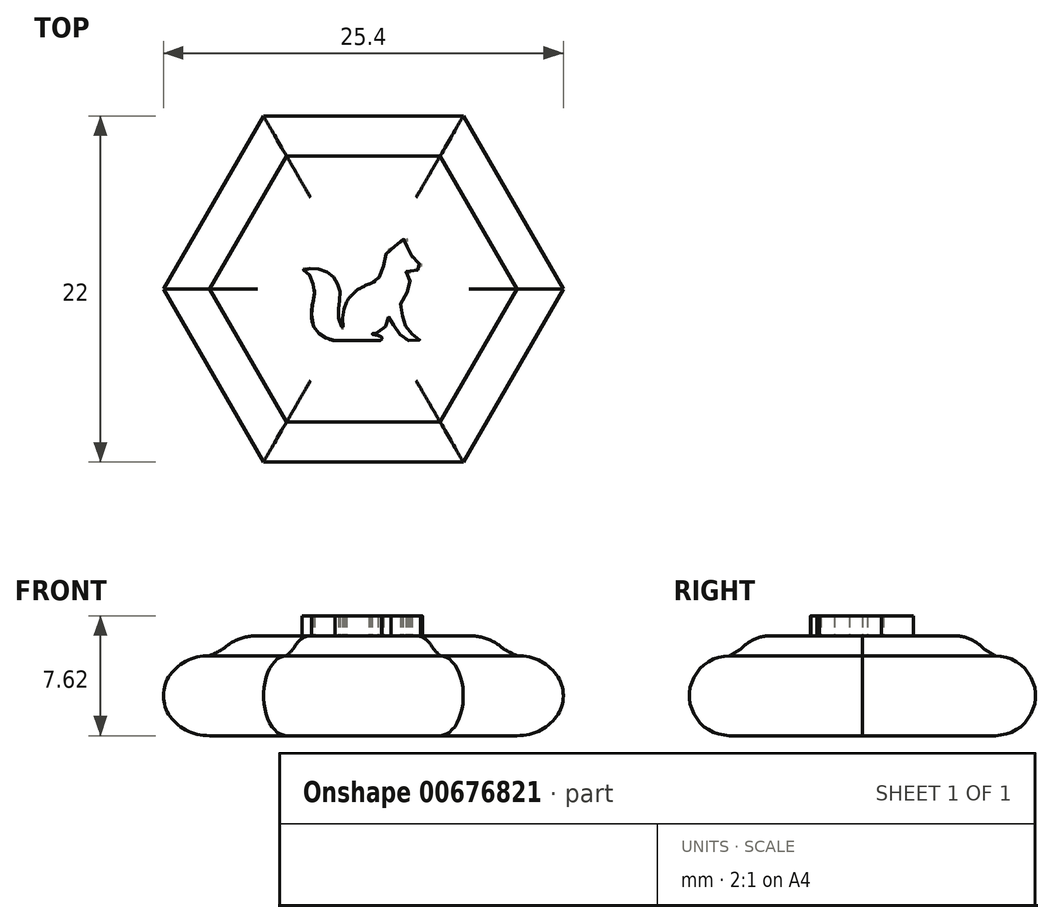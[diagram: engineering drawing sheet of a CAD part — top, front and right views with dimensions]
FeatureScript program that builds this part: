
annotation { "Feature Type Name" : "Feature", "Feature Type Description" : "" }
export const myFeature = defineFeature(function(context is Context, id is Id, definition is map)
    precondition{}
    {
        {
            var Q0;
            Q0=qCreatedBy(makeId("Front.planeOp"),FACE);
            var sketch = newSketch(context, id + "F0", { "sketchPlane" : qUnion([Q0])});
            skLineSegment(sketch, "E0", {"start": v(0, 0) * mm, "end": v(-10.16, 0) * mm});
            skLineSegment(sketch, "E1", {"start": v(-10.16, 0) * mm, "end": v(-10.16, 5.08) * mm, "construction": true});
            skLineSegment(sketch, "E2", {"start": v(10.16, 5.08) * mm, "end": v(10.16, 0) * mm, "construction": true});
            skLineSegment(sketch, "E3", {"start": v(10.16, 0) * mm, "end": v(0, 0) * mm});
            skLineSegment(sketch, "E4", {"start": v(-10.16, 5.08) * mm, "end": v(-9.2, 5.08) * mm, "construction": true});
            skLineSegment(sketch, "E5", {"start": v(-9.2, 5.08) * mm, "end": v(-8.9, 5.08) * mm, "construction": true});
            skLineSegment(sketch, "E6", {"start": v(-9.2, 5.08) * mm, "end": v(-9.2, 5.71) * mm, "construction": true});
            skLineSegment(sketch, "E7", {"start": v(-8.9, 5.08) * mm, "end": v(-8.9, 6.35) * mm, "construction": true});
            skLineSegment(sketch, "E8", {"start": v(10.16, 5.08) * mm, "end": v(9.2, 5.08) * mm, "construction": true});
            skLineSegment(sketch, "E9", {"start": v(9.2, 5.08) * mm, "end": v(8.89, 5.08) * mm, "construction": true});
            skLineSegment(sketch, "E10", {"start": v(8.89, 5.08) * mm, "end": v(8.89, 6.35) * mm, "construction": true});
            skLineSegment(sketch, "E11", {"start": v(9.2, 5.08) * mm, "end": v(9.2, 5.72) * mm, "construction": true});
            skFitSpline(sketch, "E12", {"points": [v(-10.16, 5.08) * mm, v(-9.2, 5.71) * mm, v(-8.9, 6.35) * mm], "startDerivative": vector(7.31, 1.8) * mm, "endDerivative": vector(2.53, 3.38) * mm});
            skFitSpline(sketch, "E13", {"points": [v(8.89, 6.35) * mm, v(9.2, 5.72) * mm, v(10.16, 5.08) * mm], "startDerivative": vector(2.53, -3.38) * mm, "endDerivative": vector(7.31, -1.8) * mm});
            skLineSegment(sketch, "E14", {"start": v(-7.22, 6.35) * mm, "end": v(7.22, 6.35) * mm});
            skArc(sketch, "E15.filletArc", {"start": v(9.14, 5.47) * mm, "mid": v(8.27, 6.12) * mm, "end": v(7.22, 6.35) * mm});
            skArc(sketch, "E16.filletArc", {"start": v(-7.22, 6.35) * mm, "mid": v(-8.27, 6.12) * mm, "end": v(-9.14, 5.47) * mm});
            skArc(sketch, "E17", {"start": v(10.16, 0) * mm, "mid": v(12.7, 2.54) * mm, "end": v(10.16, 5.08) * mm});
            skArc(sketch, "E18", {"start": v(-10.16, 5.08) * mm, "mid": v(-12.7, 2.54) * mm, "end": v(-10.16, 0) * mm});
            skLineSegment(sketch, "E19", {"start": v(0, 0) * mm, "end": v(0, 6.35) * mm, "construction": true});
            skLineSegment(sketch, "E20", {"start": v(10.16, 2.54) * mm, "end": v(12.7, 2.54) * mm, "construction": true});
            skSolve(sketch);
        }
        {
            var Q0;
            Q0=qSketchRegion(id+"F0",true);
            extrude(context, id + "F1", {"entities" : qUnion([Q0]), "endBound" : BoundingType.SYMMETRIC, "depth" : 25.4 * mm, "offsetDistance" : 25.4 * mm});
        }
        {
            var Q0;
            Q0=qCreatedBy(makeId("Right.planeOp"),FACE);
            var sketch = newSketch(context, id + "F2", { "sketchPlane" : qUnion([Q0])});
            skLineSegment(sketch, "E21", {"start": v(0, 0) * mm, "end": v(-8.46, 0) * mm, "construction": true});
            skLineSegment(sketch, "E22", {"start": v(0, 0) * mm, "end": v(8.46, 0) * mm, "construction": true});
            skLineSegment(sketch, "E23", {"start": v(-8.46, 0) * mm, "end": v(-8.46, 5.08) * mm, "construction": true});
            skLineSegment(sketch, "E24", {"start": v(8.46, 0) * mm, "end": v(8.46, 5.08) * mm, "construction": true});
            skLineSegment(sketch, "E25", {"start": v(-8.46, 5.08) * mm, "end": v(-7.5, 5.08) * mm, "construction": true});
            skLineSegment(sketch, "E26", {"start": v(-7.5, 5.08) * mm, "end": v(-7.19, 5.08) * mm, "construction": true});
            skLineSegment(sketch, "E27", {"start": v(-7.5, 5.08) * mm, "end": v(-7.5, 5.72) * mm, "construction": true});
            skLineSegment(sketch, "E28", {"start": v(8.46, 5.08) * mm, "end": v(7.5, 5.08) * mm, "construction": true});
            skLineSegment(sketch, "E29", {"start": v(7.5, 5.08) * mm, "end": v(7.19, 5.08) * mm, "construction": true});
            skLineSegment(sketch, "E30", {"start": v(7.5, 5.08) * mm, "end": v(7.5, 5.72) * mm, "construction": true});
            skArc(sketch, "E31", {"start": v(8.46, 0) * mm, "mid": v(11, 2.54) * mm, "end": v(8.46, 5.08) * mm});
            skArc(sketch, "E32", {"start": v(-8.46, 5.08) * mm, "mid": v(-11, 2.54) * mm, "end": v(-8.46, 0) * mm});
            skPoint(sketch, "E33.visualSharp", {"position": v(-7.19, 6.35) * mm});
            skLineSegment(sketch, "E34", {"start": v(-7.19, 5.08) * mm, "end": v(-7.19, 6.35) * mm, "construction": true});
            skPoint(sketch, "E35.visualSharp", {"position": v(7.19, 6.35) * mm});
            skLineSegment(sketch, "E36", {"start": v(7.19, 5.08) * mm, "end": v(7.19, 6.35) * mm, "construction": true});
            skLineSegment(sketch, "E37", {"start": v(0, 0) * mm, "end": v(0, 6.35) * mm, "construction": true});
            skLineSegment(sketch, "E38", {"start": v(18.44, 6.35) * mm, "end": v(18.44, 0) * mm});
            skLineSegment(sketch, "E39", {"start": v(-18.44, 6.35) * mm, "end": v(-18.44, 0) * mm});
            skLineSegment(sketch, "E40", {"start": v(-8.46, 0) * mm, "end": v(-18.44, 0) * mm});
            skLineSegment(sketch, "E41", {"start": v(-8.46, 2.54) * mm, "end": v(-11, 2.54) * mm, "construction": true});
            skLineSegment(sketch, "E42", {"start": v(18.44, 0) * mm, "end": v(8.46, 0) * mm});
            skLineSegment(sketch, "E43", {"start": v(0, 0) * mm, "end": v(0, 0) * mm});
            skLineSegment(sketch, "E44", {"start": v(-5.82, 6.35) * mm, "end": v(5.82, 6.35) * mm});
            skFitSpline(sketch, "E45", {"points": [v(-8.46, 5.08) * mm, v(-7.5, 5.71) * mm, v(-7.19, 6.35) * mm], "startDerivative": vector(1.98, 1.05) * mm, "endDerivative": vector(0.5, 1.5) * mm});
            skFitSpline(sketch, "E46", {"points": [v(7.19, 6.35) * mm, v(7.5, 5.71) * mm, v(8.46, 5.08) * mm], "startDerivative": vector(0.5, -1.5) * mm, "endDerivative": vector(1.98, -1.05) * mm});
            skArc(sketch, "E47.filletArc", {"start": v(-5.82, 6.35) * mm, "mid": v(-6.76, 6.17) * mm, "end": v(-7.58, 5.64) * mm});
            skArc(sketch, "E48.filletArc", {"start": v(7.58, 5.64) * mm, "mid": v(6.76, 6.17) * mm, "end": v(5.82, 6.35) * mm});
            skLineSegment(sketch, "E49", {"start": v(-18.44, 6.35) * mm, "end": v(-5.82, 6.35) * mm});
            skLineSegment(sketch, "E50", {"start": v(5.82, 6.35) * mm, "end": v(18.44, 6.35) * mm});
            skSolve(sketch);
        }
        {
            var Q0;
            Q0=qSketchRegion(id+"F2",true);
            extrude(context, id + "F3", {"entities" : qUnion([Q0]), "operationType" : NewBodyOperationType.REMOVE, "endBound" : BoundingType.SYMMETRIC, "depth" : 25.4 * mm, "offsetDistance" : 25.4 * mm});
        }
        {
            var Q0;
            Q0=sQuery(id+"F0.wireOp",EDGE,"E19");
            cPlane(context, id + "F4", {"entities" : qUnion([Q0]), "cplaneType" : CPlaneType.LINE_ANGLE, "offset" : 25.4 * mm, "angle" : 120 * degree, "width" : 152.4 * mm, "height" : 152.4 * mm});
        }
        {
            var Q0;
            Q0=qCreatedBy(id+"F4.planeOp",FACE);
            var sketch = newSketch(context, id + "F5", { "sketchPlane" : qUnion([Q0])});
            skLineSegment(sketch, "E51", {"start": v(0, 0) * mm, "end": v(-8.46, 0) * mm, "construction": true});
            skLineSegment(sketch, "E52", {"start": v(0, 0) * mm, "end": v(8.46, 0) * mm, "construction": true});
            skLineSegment(sketch, "E53", {"start": v(-8.46, 0) * mm, "end": v(-8.46, 5.08) * mm, "construction": true});
            skLineSegment(sketch, "E54", {"start": v(8.46, 0) * mm, "end": v(8.46, 5.08) * mm, "construction": true});
            skLineSegment(sketch, "E55", {"start": v(-8.46, 5.08) * mm, "end": v(-7.5, 5.08) * mm, "construction": true});
            skLineSegment(sketch, "E56", {"start": v(-7.5, 5.08) * mm, "end": v(-7.19, 5.08) * mm, "construction": true});
            skLineSegment(sketch, "E57", {"start": v(-7.5, 5.08) * mm, "end": v(-7.5, 5.72) * mm, "construction": true});
            skLineSegment(sketch, "E58", {"start": v(8.46, 5.08) * mm, "end": v(7.5, 5.08) * mm, "construction": true});
            skLineSegment(sketch, "E59", {"start": v(7.5, 5.08) * mm, "end": v(7.19, 5.08) * mm, "construction": true});
            skLineSegment(sketch, "E60", {"start": v(7.5, 5.08) * mm, "end": v(7.5, 5.72) * mm, "construction": true});
            skArc(sketch, "E61", {"start": v(8.46, 0) * mm, "mid": v(11, 2.54) * mm, "end": v(8.46, 5.08) * mm});
            skArc(sketch, "E62", {"start": v(-8.46, 5.08) * mm, "mid": v(-11, 2.54) * mm, "end": v(-8.46, 0) * mm});
            skPoint(sketch, "E63.visualSharp", {"position": v(-7.19, 6.35) * mm});
            skLineSegment(sketch, "E64", {"start": v(-7.19, 5.08) * mm, "end": v(-7.19, 6.35) * mm, "construction": true});
            skPoint(sketch, "E65.visualSharp", {"position": v(7.19, 6.35) * mm});
            skLineSegment(sketch, "E66", {"start": v(7.19, 5.08) * mm, "end": v(7.19, 6.35) * mm, "construction": true});
            skLineSegment(sketch, "E67", {"start": v(0, 0) * mm, "end": v(0, 6.35) * mm, "construction": true});
            skLineSegment(sketch, "E68", {"start": v(18.44, 6.35) * mm, "end": v(18.44, 0) * mm});
            skLineSegment(sketch, "E69", {"start": v(-18.44, 6.35) * mm, "end": v(-18.44, 0) * mm});
            skLineSegment(sketch, "E70", {"start": v(-8.46, 0) * mm, "end": v(-18.44, 0) * mm});
            skLineSegment(sketch, "E71", {"start": v(-8.46, 2.54) * mm, "end": v(-11, 2.54) * mm, "construction": true});
            skLineSegment(sketch, "E72", {"start": v(18.44, 0) * mm, "end": v(8.46, 0) * mm});
            skLineSegment(sketch, "E73", {"start": v(0, 0) * mm, "end": v(0, 0) * mm});
            skLineSegment(sketch, "E74", {"start": v(-5.82, 6.35) * mm, "end": v(5.82, 6.35) * mm});
            skFitSpline(sketch, "E75", {"points": [v(-8.46, 5.08) * mm, v(-7.5, 5.71) * mm, v(-7.19, 6.35) * mm], "startDerivative": vector(1.98, 1.05) * mm, "endDerivative": vector(0.5, 1.5) * mm});
            skFitSpline(sketch, "E76", {"points": [v(7.19, 6.35) * mm, v(7.5, 5.71) * mm, v(8.46, 5.08) * mm], "startDerivative": vector(0.5, -1.5) * mm, "endDerivative": vector(1.98, -1.05) * mm});
            skArc(sketch, "E77.filletArc", {"start": v(-5.82, 6.35) * mm, "mid": v(-6.76, 6.17) * mm, "end": v(-7.58, 5.64) * mm});
            skArc(sketch, "E78.filletArc", {"start": v(7.58, 5.64) * mm, "mid": v(6.76, 6.17) * mm, "end": v(5.82, 6.35) * mm});
            skLineSegment(sketch, "E79", {"start": v(-18.44, 6.35) * mm, "end": v(-5.82, 6.35) * mm});
            skLineSegment(sketch, "E80", {"start": v(5.82, 6.35) * mm, "end": v(18.44, 6.35) * mm});
            skSolve(sketch);
        }
        {
            var Q0;
            Q0=qSketchRegion(id+"F5",true);
            var Q1;
            Q1=sQuery(id+"FHUch5MhYWofbFd_1.wireOp",EDGE,"UJUXWhbe-ns99-R938-MBjs-qnEI7qI75ZtX");
            var Q2;
            Q2=sQuery(id+"FHUch5MhYWofbFd_1.wireOp",EDGE,"TGRI2bbO-5mKc-ZYGL-RI2u-ax8UZepCr2S6");
            var Q3;
            Q3=sQuery(id+"FHUch5MhYWofbFd_1.wireOp",EDGE,"3EN97P5a-7fpQ-fkxS-kFIG-O94JdEreBvdc");
            var Q4;
            Q4=sQuery(id+"FHUch5MhYWofbFd_1.wireOp",EDGE,"BLXI86f6-p3FV-xg8e-vcjV-MuaEN1ZbEeBN");
            var Q5;
            Q5=sQuery(id+"FHUch5MhYWofbFd_1.wireOp",EDGE,"K6Pg9hkI-HhUm-eWt8-lgsy-rQcUfMNRkeRX");
            var Q6;
            Q6=sQuery(id+"FHUch5MhYWofbFd_1.wireOp",EDGE,"8MWXePed-qfWZ-9kiI-xQLn-RgFZeWpe4DeW");
            var Q7;
            Q7=sQuery(id+"FHUch5MhYWofbFd_1.wireOp",EDGE,"ujHeR1Bt-oqxH-zWrO-aF7a-1cGxx1oxEC4p");
            var Q8;
            Q8=sQuery(id+"FHUch5MhYWofbFd_1.wireOp",EDGE,"ezDig2bh-fpcZ-qdXg-hfEw-k3bdO8GFTHoY");
            var Q9;
            Q9=sQuery(id+"FHUch5MhYWofbFd_1.wireOp",EDGE,"TL3t9Hpy-tibO-WM6d-k033-ZjCVjvvUcohB");
            var Q10;
            Q10=sQuery(id+"FHUch5MhYWofbFd_1.wireOp",EDGE,"H6XLH3zd-cpDk-JRaX-qujs-Kg6a5HbhHDUq");
            var Q11;
            Q11=sQuery(id+"FHUch5MhYWofbFd_1.wireOp",EDGE,"XlrNxneH-uq2I-L97s-EfPg-StDvBexp0ezL");
            var Q12;
            Q12=sQuery(id+"FHUch5MhYWofbFd_1.wireOp",EDGE,"V9PWrxtB-5fyD-G3Op-kF2t-xwj5HEO20ic1");
            var Q13;
            Q13=sQuery(id+"FHUch5MhYWofbFd_1.wireOp",EDGE,"DBsLzJAx-6rkW-YoXi-OfuC-MLqgEexGkzpa");
            extrude(context, id + "F6", {"entities" : qUnion([Q0]), "operationType" : NewBodyOperationType.REMOVE, "surfaceEntities" : qUnion([Q1, Q2, Q3, Q4, Q5, Q6, Q7, Q8, Q9, Q10, Q11, Q12, Q13]), "endBound" : BoundingType.SYMMETRIC, "oppositeDirection" : true, "depth" : 50.8 * mm, "offsetDistance" : 25.4 * mm});
        }
        {
            var Q0;
            Q0=sQuery(id+"F0.wireOp",EDGE,"E19");
            cPlane(context, id + "F7", {"entities" : qUnion([Q0]), "cplaneType" : CPlaneType.LINE_ANGLE, "offset" : 25.4 * mm, "angle" : 60 * degree, "width" : 152.4 * mm, "height" : 152.4 * mm});
        }
        {
            var Q0;
            Q0=qCreatedBy(id+"F7.planeOp",FACE);
            var sketch = newSketch(context, id + "F8", { "sketchPlane" : qUnion([Q0])});
            skLineSegment(sketch, "E81", {"start": v(0, 0) * mm, "end": v(-8.46, 0) * mm, "construction": true});
            skLineSegment(sketch, "E82", {"start": v(0, 0) * mm, "end": v(8.46, 0) * mm, "construction": true});
            skLineSegment(sketch, "E83", {"start": v(-8.46, 0) * mm, "end": v(-8.46, 5.08) * mm, "construction": true});
            skLineSegment(sketch, "E84", {"start": v(8.46, 0) * mm, "end": v(8.46, 5.08) * mm, "construction": true});
            skLineSegment(sketch, "E85", {"start": v(-8.46, 5.08) * mm, "end": v(-7.5, 5.08) * mm, "construction": true});
            skLineSegment(sketch, "E86", {"start": v(-7.5, 5.08) * mm, "end": v(-7.19, 5.08) * mm, "construction": true});
            skLineSegment(sketch, "E87", {"start": v(-7.5, 5.08) * mm, "end": v(-7.5, 5.71) * mm, "construction": true});
            skLineSegment(sketch, "E88", {"start": v(8.46, 5.08) * mm, "end": v(7.5, 5.08) * mm, "construction": true});
            skLineSegment(sketch, "E89", {"start": v(7.5, 5.08) * mm, "end": v(7.19, 5.08) * mm, "construction": true});
            skLineSegment(sketch, "E90", {"start": v(7.5, 5.08) * mm, "end": v(7.5, 5.71) * mm, "construction": true});
            skArc(sketch, "E91", {"start": v(8.46, 0) * mm, "mid": v(11, 2.54) * mm, "end": v(8.46, 5.08) * mm});
            skArc(sketch, "E92", {"start": v(-8.46, 5.08) * mm, "mid": v(-11, 2.54) * mm, "end": v(-8.46, 0) * mm});
            skPoint(sketch, "E93.visualSharp", {"position": v(-7.19, 6.35) * mm});
            skLineSegment(sketch, "E94", {"start": v(-7.19, 5.08) * mm, "end": v(-7.19, 6.35) * mm, "construction": true});
            skPoint(sketch, "E95.visualSharp", {"position": v(7.19, 6.35) * mm});
            skLineSegment(sketch, "E96", {"start": v(7.19, 5.08) * mm, "end": v(7.19, 6.35) * mm, "construction": true});
            skLineSegment(sketch, "E97", {"start": v(0, 0) * mm, "end": v(0, 6.35) * mm, "construction": true});
            skLineSegment(sketch, "E98", {"start": v(18.44, 6.35) * mm, "end": v(18.44, 0) * mm});
            skLineSegment(sketch, "E99", {"start": v(-18.44, 6.35) * mm, "end": v(-18.44, 0) * mm});
            skLineSegment(sketch, "E100", {"start": v(-8.46, 0) * mm, "end": v(-18.44, 0) * mm});
            skLineSegment(sketch, "E101", {"start": v(-8.46, 2.54) * mm, "end": v(-11, 2.54) * mm, "construction": true});
            skLineSegment(sketch, "E102", {"start": v(18.44, 0) * mm, "end": v(8.46, 0) * mm});
            skLineSegment(sketch, "E103", {"start": v(0, 0) * mm, "end": v(0, 0) * mm});
            skLineSegment(sketch, "E104", {"start": v(-5.82, 6.35) * mm, "end": v(5.82, 6.35) * mm});
            skFitSpline(sketch, "E105", {"points": [v(-8.46, 5.08) * mm, v(-7.5, 5.71) * mm, v(-7.19, 6.35) * mm], "startDerivative": vector(1.98, 1.05) * mm, "endDerivative": vector(0.5, 1.5) * mm});
            skFitSpline(sketch, "E106", {"points": [v(7.19, 6.35) * mm, v(7.5, 5.71) * mm, v(8.46, 5.08) * mm], "startDerivative": vector(0.5, -1.5) * mm, "endDerivative": vector(1.98, -1.05) * mm});
            skArc(sketch, "E107.filletArc", {"start": v(-5.82, 6.35) * mm, "mid": v(-6.76, 6.17) * mm, "end": v(-7.58, 5.64) * mm});
            skArc(sketch, "E108.filletArc", {"start": v(7.58, 5.64) * mm, "mid": v(6.76, 6.17) * mm, "end": v(5.82, 6.35) * mm});
            skLineSegment(sketch, "E109", {"start": v(-18.44, 6.35) * mm, "end": v(-5.82, 6.35) * mm});
            skLineSegment(sketch, "E110", {"start": v(5.82, 6.35) * mm, "end": v(18.44, 6.35) * mm});
            skSolve(sketch);
        }
        {
            var Q0;
            Q0=qSketchRegion(id+"F8",true);
            extrude(context, id + "F9", {"entities" : qUnion([Q0]), "operationType" : NewBodyOperationType.REMOVE, "endBound" : BoundingType.SYMMETRIC, "oppositeDirection" : true, "depth" : 25.4 * mm, "offsetDistance" : 25.4 * mm});
        }
        {
            var Q0;
            Q0=makeQuery(id+"F1.opExtrude","SWEPT_FACE",FACE,{"disambiguationData":[OSD([sQuery(id+"F0.wireOp",EDGE,"E14")])]});
            var sketch = newSketch(context, id + "F10", { "sketchPlane" : qUnion([Q0])});
            skLineSegment(sketch, "E111", {"start": v(6.72, 0) * mm, "end": v(3.36, 5.82) * mm, "construction": true});
            skLineSegment(sketch, "E112", {"start": v(3.36, 5.82) * mm, "end": v(-3.36, 5.82) * mm, "construction": true});
            skLineSegment(sketch, "E113", {"start": v(-3.36, 5.82) * mm, "end": v(-6.72, 0) * mm, "construction": true});
            skLineSegment(sketch, "E114", {"start": v(-6.72, 0) * mm, "end": v(-3.36, -5.82) * mm, "construction": true});
            skLineSegment(sketch, "E115", {"start": v(-3.36, -5.82) * mm, "end": v(3.36, -5.82) * mm, "construction": true});
            skLineSegment(sketch, "E116", {"start": v(3.36, -5.82) * mm, "end": v(6.72, 0) * mm, "construction": true});
            skLineSegment(sketch, "E117", {"start": v(0, 0) * mm, "end": v(0, 0) * mm});
            skLineSegment(sketch, "E118", {"start": v(-4.26, 4.26) * mm, "end": v(4.26, 4.26) * mm, "construction": true});
            skLineSegment(sketch, "E119", {"start": v(4.26, 4.26) * mm, "end": v(4.26, -4.26) * mm, "construction": true});
            skLineSegment(sketch, "E120", {"start": v(4.26, -4.26) * mm, "end": v(-4.26, -4.26) * mm, "construction": true});
            skLineSegment(sketch, "E121", {"start": v(-4.26, -4.26) * mm, "end": v(-4.26, 4.26) * mm, "construction": true});
            skFitSpline(sketch, "E122", {"points": [v(-1.8, -3.28) * mm, v(-1.7, -3.29) * mm, v(-1.6, -3.29) * mm, v(-1.54, -3.29) * mm, v(-1.42, -3.29) * mm, v(-1.32, -3.29) * mm, v(-1.23, -3.29) * mm, v(-1.17, -3.29) * mm, v(-1.12, -3.29) * mm, v(-1.02, -3.29) * mm, v(-0.94, -3.29) * mm, v(-0.9, -3.29) * mm, v(-0.85, -3.29) * mm, v(-0.78, -3.29) * mm, v(-0.76, -3.29) * mm, v(-0.66, -3.29) * mm, v(-0.45, -3.29) * mm, v(-0.33, -3.29) * mm, v(-0.25, -3.29) * mm, v(-0.16, -3.29) * mm, v(-0.08, -3.29) * mm, v(0, -3.29) * mm, v(0.12, -3.29) * mm, v(0.21, -3.29) * mm, v(0.3, -3.29) * mm, v(0.39, -3.28) * mm, v(0.49, -3.28) * mm, v(0.6, -3.28) * mm, v(0.69, -3.28) * mm, v(0.78, -3.28) * mm, v(0.87, -3.28) * mm, v(0.99, -3.28) * mm, v(1.09, -3.28) * mm, v(1.11, -3.24) * mm, v(1.15, -3.21) * mm, v(1.17, -3.17) * mm, v(1.17, -3.15) * mm, v(1.2, -3.11) * mm, v(1.17, -3.06) * mm, v(1.14, -3.04) * mm, v(1.11, -3.02) * mm, v(1.05, -3) * mm, v(1.02, -2.98) * mm, v(0.96, -2.95) * mm, v(0.9, -2.94) * mm, v(0.87, -2.93) * mm, v(0.82, -2.93) * mm, v(0.8, -2.91) * mm, v(0.76, -2.91) * mm, v(0.73, -2.9) * mm, v(0.7, -2.9) * mm, v(0.65, -2.9) * mm, v(0.62, -2.9) * mm, v(0.6, -2.9) * mm, v(0.56, -2.89) * mm, v(0.55, -2.88) * mm, v(0.55, -2.85) * mm, v(0.55, -2.84) * mm, v(0.58, -2.83) * mm, v(0.6, -2.83) * mm, v(0.64, -2.83) * mm, v(0.67, -2.83) * mm, v(0.68, -2.82) * mm, v(0.7, -2.82) * mm, v(0.73, -2.82) * mm, v(0.76, -2.82) * mm, v(0.81, -2.8) * mm, v(0.85, -2.77) * mm, v(0.89, -2.75) * mm, v(0.9, -2.74) * mm, v(0.93, -2.74) * mm, v(0.93, -2.74) * mm], "startDerivative": vector(5, -0.43) * mm, "endDerivative": vector(0.95, 0.05) * mm});
            skFitSpline(sketch, "E123", {"points": [v(0.93, -2.74) * mm, v(0.99, -2.74) * mm, v(1.02, -2.69) * mm, v(1.06, -2.67) * mm, v(1.1, -2.64) * mm, v(1.13, -2.61) * mm, v(1.16, -2.59) * mm, v(1.19, -2.56) * mm, v(1.21, -2.55) * mm, v(1.25, -2.52) * mm, v(1.28, -2.5) * mm, v(1.3, -2.47) * mm, v(1.32, -2.46) * mm, v(1.34, -2.43) * mm, v(1.35, -2.41) * mm, v(1.38, -2.39) * mm, v(1.4, -2.37) * mm, v(1.45, -2.34) * mm, v(1.45, -2.32) * mm, v(1.46, -2.3) * mm, v(1.48, -2.26) * mm, v(1.51, -2.2) * mm, v(1.53, -2.16) * mm, v(1.54, -2.11) * mm, v(1.56, -2.07) * mm, v(1.58, -2.02) * mm, v(1.58, -1.99) * mm, v(1.58, -1.96) * mm, v(1.59, -1.94) * mm, v(1.6, -1.9) * mm, v(1.6, -1.84) * mm, v(1.62, -1.8) * mm, v(1.62, -1.77) * mm, v(1.64, -1.77) * mm, v(1.65, -1.8) * mm, v(1.66, -1.81) * mm, v(1.68, -1.85) * mm, v(1.7, -1.9) * mm, v(1.72, -1.95) * mm, v(1.75, -1.98) * mm, v(1.75, -2.01) * mm, v(1.81, -2.06) * mm, v(1.82, -2.08) * mm, v(1.84, -2.13) * mm, v(1.88, -2.2) * mm, v(1.9, -2.25) * mm, v(1.9, -2.27) * mm, v(1.92, -2.29) * mm, v(1.94, -2.3) * mm, v(1.97, -2.34) * mm, v(2, -2.39) * mm, v(2.05, -2.43) * mm, v(2.07, -2.5) * mm, v(2.11, -2.55) * mm, v(2.14, -2.6) * mm, v(2.17, -2.64) * mm, v(2.2, -2.7) * mm, v(2.25, -2.74) * mm, v(2.27, -2.81) * mm, v(2.3, -2.85) * mm, v(2.33, -2.87) * mm, v(2.4, -2.95) * mm, v(2.42, -3) * mm, v(2.45, -3.02) * mm, v(2.48, -3.05) * mm, v(2.5, -3.09) * mm, v(2.53, -3.1) * mm, v(2.54, -3.12) * mm, v(2.58, -3.17) * mm, v(2.66, -3.23) * mm, v(2.69, -3.24) * mm, v(2.7, -3.26) * mm, v(2.7, -3.26) * mm, v(2.75, -3.28) * mm, v(2.82, -3.28) * mm, v(2.9, -3.28) * mm, v(2.95, -3.28) * mm, v(2.97, -3.28) * mm, v(3.02, -3.28) * mm, v(3.06, -3.28) * mm, v(3.13, -3.3) * mm, v(3.18, -3.29) * mm, v(3.25, -3.28) * mm, v(3.32, -3.28) * mm, v(3.4, -3.28) * mm, v(3.49, -3.28) * mm, v(3.53, -3.28) * mm, v(3.54, -3.25) * mm, v(3.57, -3.23) * mm, v(3.6, -3.19) * mm, v(3.63, -3.16) * mm, v(3.64, -3.08) * mm, v(3.64, -3.01) * mm, v(3.55, -2.92) * mm, v(3.48, -2.9) * mm, v(3.37, -2.9) * mm, v(3.28, -2.9) * mm, v(3.2, -2.9) * mm, v(3.17, -2.9) * mm, v(3.13, -2.9) * mm, v(3.1, -2.88) * mm, v(3.06, -2.85) * mm, v(3.04, -2.81) * mm, v(3.02, -2.8) * mm, v(3, -2.74) * mm, v(2.96, -2.74) * mm, v(2.95, -2.7) * mm, v(2.91, -2.65) * mm, v(2.87, -2.6) * mm, v(2.86, -2.59) * mm, v(2.86, -2.58) * mm, v(2.82, -2.5) * mm, v(2.78, -2.45) * mm, v(2.77, -2.42) * mm, v(2.74, -2.39) * mm, v(2.7, -2.35) * mm, v(2.66, -2.3) * mm, v(2.64, -2.27) * mm, v(2.64, -2.21) * mm, v(2.62, -2.18) * mm, v(2.6, -2.14) * mm, v(2.58, -2.1) * mm, v(2.58, -2.06) * mm, v(2.56, -2.03) * mm, v(2.53, -1.97) * mm, v(2.53, -1.94) * mm, v(2.53, -1.91) * mm, v(2.48, -1.86) * mm, v(2.48, -1.79) * mm, v(2.48, -1.74) * mm, v(2.46, -1.7) * mm, v(2.4, -1.62) * mm, v(2.4, -1.5) * mm, v(2.4, -1.43) * mm, v(2.4, -1.4) * mm, v(2.4, -1.37) * mm, v(2.4, -1.35) * mm, v(2.39, -1.25) * mm, v(2.39, -1.2) * mm, v(2.39, -1.17) * mm, v(2.39, -1.12) * mm, v(2.37, -1.03) * mm, v(2.37, -0.99) * mm, v(2.39, -0.92) * mm, v(2.4, -0.85) * mm, v(2.42, -0.8) * mm, v(2.48, -0.75) * mm, v(2.52, -0.67) * mm, v(2.56, -0.6) * mm, v(2.58, -0.57) * mm, v(2.61, -0.5) * mm, v(2.65, -0.41) * mm, v(2.7, -0.34) * mm, v(2.75, -0.3) * mm, v(2.77, -0.2) * mm, v(2.8, -0.2) * mm, v(2.82, -0.13) * mm, v(2.86, 0) * mm, v(2.9, 0.05) * mm, v(2.92, 0.1) * mm, v(2.94, 0.15) * mm, v(2.94, 0.18) * mm, v(2.94, 0.24) * mm, v(2.95, 0.3) * mm, v(2.95, 0.35) * mm, v(2.95, 0.38) * mm, v(2.96, 0.43) * mm, v(2.97, 0.52) * mm, v(2.97, 0.57) * mm, v(2.97, 0.6) * mm, v(2.95, 0.63) * mm, v(2.93, 0.67) * mm, v(2.91, 0.75) * mm, v(2.9, 0.8) * mm, v(2.88, 0.83) * mm, v(2.87, 0.86) * mm, v(2.83, 0.92) * mm, v(2.8, 0.97) * mm, v(2.79, 1) * mm, v(2.77, 1.03) * mm, v(2.74, 1.06) * mm, v(2.72, 1.1) * mm, v(2.78, 1.13) * mm, v(2.84, 1.17) * mm, v(2.89, 1.19) * mm, v(2.93, 1.22) * mm, v(2.99, 1.22) * mm, v(3.05, 1.22) * mm, v(3.1, 1.22) * mm, v(3.17, 1.22) * mm, v(3.23, 1.21) * mm, v(3.33, 1.21) * mm, v(3.38, 1.21) * mm, v(3.43, 1.21) * mm, v(3.46, 1.21) * mm, v(3.53, 1.23) * mm, v(3.56, 1.26) * mm, v(3.6, 1.28) * mm, v(3.65, 1.3) * mm, v(3.71, 1.34) * mm, v(3.74, 1.38) * mm, v(3.75, 1.43) * mm, v(3.75, 1.47) * mm, v(3.72, 1.52) * mm, v(3.64, 1.53) * mm, v(3.62, 1.56) * mm, v(3.58, 1.57) * mm, v(3.56, 1.6) * mm, v(3.5, 1.63) * mm, v(3.45, 1.64) * mm, v(3.42, 1.66) * mm, v(3.39, 1.69) * mm, v(3.35, 1.7) * mm, v(3.31, 1.73) * mm, v(3.27, 1.76) * mm, v(3.21, 1.81) * mm, v(3.19, 1.85) * mm, v(3.14, 1.9) * mm, v(3.12, 1.94) * mm, v(3.1, 1.99) * mm, v(3.08, 2.05) * mm, v(3.07, 2.12) * mm, v(3.04, 2.18) * mm, v(3.03, 2.25) * mm, v(3.03, 2.3) * mm, v(3, 2.31) * mm, v(2.98, 2.35) * mm, v(2.96, 2.37) * mm, v(2.92, 2.44) * mm, v(2.87, 2.46) * mm, v(2.83, 2.5) * mm, v(2.8, 2.52) * mm, v(2.77, 2.53) * mm, v(2.75, 2.55) * mm, v(2.76, 2.67) * mm, v(2.77, 2.73) * mm, v(2.77, 2.8) * mm, v(2.8, 2.88) * mm, v(2.8, 2.95) * mm, v(2.8, 3.02) * mm, v(2.8, 3.1) * mm, v(2.8, 3.15) * mm, v(2.8, 3.18) * mm, v(2.8, 3.2) * mm, v(2.74, 3.24) * mm, v(2.68, 3.21) * mm, v(2.64, 3.2) * mm, v(2.61, 3.2) * mm, v(2.56, 3.15) * mm, v(2.52, 3.12) * mm, v(2.48, 3.07) * mm, v(2.43, 3.04) * mm, v(2.37, 3) * mm, v(2.35, 2.97) * mm, v(2.32, 2.94) * mm, v(2.27, 2.89) * mm, v(2.22, 2.85) * mm, v(2.16, 2.8) * mm, v(2.1, 2.74) * mm, v(2.09, 2.7) * mm, v(2.02, 2.7) * mm, v(1.96, 2.68) * mm, v(1.9, 2.68) * mm, v(1.84, 2.66) * mm, v(1.8, 2.63) * mm, v(1.74, 2.59) * mm, v(1.7, 2.56) * mm, v(1.65, 2.53) * mm, v(1.6, 2.48) * mm, v(1.57, 2.44) * mm, v(1.56, 2.4) * mm, v(1.52, 2.38) * mm, v(1.48, 2.3) * mm, v(1.44, 2.25) * mm, v(1.4, 2.17) * mm, v(1.38, 2.11) * mm, v(1.36, 2.06) * mm, v(1.34, 2) * mm, v(1.32, 1.96) * mm, v(1.3, 1.88) * mm, v(1.29, 1.8) * mm, v(1.28, 1.75) * mm, v(1.28, 1.7) * mm, v(1.27, 1.66) * mm, v(1.27, 1.6) * mm, v(1.27, 1.51) * mm, v(1.27, 1.43) * mm, v(1.27, 1.37) * mm, v(1.25, 1.27) * mm, v(1.22, 1.21) * mm, v(1.2, 1.13) * mm, v(1.17, 1.08) * mm, v(1.15, 1) * mm, v(1.11, 0.9) * mm, v(1.1, 0.86) * mm, v(1.08, 0.83) * mm, v(1.05, 0.78) * mm, v(1, 0.73) * mm, v(0.98, 0.7) * mm, v(0.93, 0.67) * mm, v(0.9, 0.61) * mm, v(0.88, 0.58) * mm, v(0.83, 0.53) * mm, v(0.8, 0.51) * mm, v(0.77, 0.5) * mm, v(0.73, 0.46) * mm, v(0.69, 0.45) * mm, v(0.64, 0.44) * mm, v(0.56, 0.4) * mm, v(0.52, 0.38) * mm, v(0.46, 0.35) * mm, v(0.41, 0.33) * mm, v(0.41, 0.33) * mm], "startDerivative": vector(17.88, -4.57) * mm, "endDerivative": vector(-2.96, 0.86) * mm});
            skFitSpline(sketch, "E124", {"points": [v(0.35, 0.32) * mm, v(0.26, 0.28) * mm, v(0.21, 0.27) * mm, v(0.17, 0.24) * mm, v(0.12, 0.2) * mm, v(0.04, 0.16) * mm, v(-0.03, 0.13) * mm, v(-0.07, 0.1) * mm, v(-0.14, 0.08) * mm, v(-0.2, 0.03) * mm, v(-0.28, 0) * mm, v(-0.32, 0) * mm, v(-0.37, -0.06) * mm, v(-0.4, -0.08) * mm, v(-0.43, -0.1) * mm, v(-0.46, -0.13) * mm, v(-0.5, -0.15) * mm, v(-0.52, -0.18) * mm, v(-0.55, -0.2) * mm, v(-0.61, -0.27) * mm, v(-0.66, -0.32) * mm, v(-0.71, -0.36) * mm, v(-0.76, -0.41) * mm, v(-0.8, -0.45) * mm, v(-0.82, -0.47) * mm, v(-0.84, -0.5) * mm, v(-0.86, -0.52) * mm, v(-0.88, -0.54) * mm, v(-0.9, -0.57) * mm, v(-0.93, -0.6) * mm, v(-0.95, -0.67) * mm, v(-0.98, -0.7) * mm, v(-1, -0.76) * mm, v(-1.06, -0.81) * mm], "startDerivative": vector(-2.2, -1.25) * mm, "endDerivative": vector(-1.74, -1.28) * mm});
            skFitSpline(sketch, "E125", {"points": [v(0.35, 0.32) * mm, v(0.41, 0.33) * mm], "startDerivative": vector(0.07, 0) * mm, "endDerivative": vector(0.07, 0) * mm});
            skFitSpline(sketch, "E126", {"points": [v(-1.06, -0.81) * mm, v(-1.09, -0.87) * mm, v(-1.1, -0.92) * mm, v(-1.1, -0.95) * mm, v(-1.12, -0.99) * mm, v(-1.15, -1.02) * mm, v(-1.17, -1.08) * mm, v(-1.19, -1.12) * mm, v(-1.2, -1.17) * mm, v(-1.21, -1.23) * mm, v(-1.22, -1.31) * mm, v(-1.26, -1.38) * mm, v(-1.27, -1.45) * mm, v(-1.27, -1.53) * mm, v(-1.28, -1.59) * mm, v(-1.29, -1.66) * mm, v(-1.3, -1.72) * mm, v(-1.3, -1.83) * mm, v(-1.31, -1.93) * mm, v(-1.31, -2.01) * mm, v(-1.31, -2.08) * mm, v(-1.3, -2.1) * mm, v(-1.3, -2.17) * mm, v(-1.3, -2.24) * mm, v(-1.3, -2.3) * mm, v(-1.3, -2.38) * mm, v(-1.27, -2.45) * mm, v(-1.25, -2.5) * mm, v(-1.25, -2.6) * mm, v(-1.25, -2.62) * mm, v(-1.3, -2.6) * mm, v(-1.3, -2.57) * mm, v(-1.35, -2.5) * mm, v(-1.37, -2.44) * mm, v(-1.4, -2.39) * mm, v(-1.43, -2.33) * mm, v(-1.46, -2.28) * mm, v(-1.48, -2.2) * mm, v(-1.51, -2.12) * mm, v(-1.52, -2.05) * mm, v(-1.53, -1.97) * mm, v(-1.54, -1.88) * mm, v(-1.57, -1.82) * mm, v(-1.58, -1.73) * mm, v(-1.58, -1.66) * mm, v(-1.58, -1.56) * mm, v(-1.58, -1.49) * mm, v(-1.58, -1.43) * mm, v(-1.58, -1.37) * mm, v(-1.58, -1.32) * mm, v(-1.58, -1.28) * mm, v(-1.58, -1.22) * mm, v(-1.58, -1.17) * mm, v(-1.56, -1.12) * mm, v(-1.56, -1.06) * mm, v(-1.56, -1.01) * mm, v(-1.56, -0.94) * mm, v(-1.55, -0.81) * mm, v(-1.52, -0.76) * mm, v(-1.5, -0.67) * mm, v(-1.5, -0.63) * mm, v(-1.5, -0.56) * mm, v(-1.5, -0.45) * mm, v(-1.5, -0.4) * mm, v(-1.5, -0.33) * mm, v(-1.5, -0.26) * mm, v(-1.5, -0.2) * mm, v(-1.5, -0.11) * mm, v(-1.52, -0.06) * mm, v(-1.53, 0) * mm, v(-1.54, 0.05) * mm, v(-1.56, 0.12) * mm, v(-1.58, 0.18) * mm, v(-1.6, 0.21) * mm, v(-1.6, 0.27) * mm, v(-1.64, 0.32) * mm, v(-1.67, 0.38) * mm, v(-1.7, 0.44) * mm, v(-1.71, 0.49) * mm, v(-1.74, 0.54) * mm, v(-1.8, 0.58) * mm, v(-1.8, 0.64) * mm, v(-1.82, 0.68) * mm, v(-1.85, 0.75) * mm, v(-1.91, 0.77) * mm, v(-1.95, 0.82) * mm, v(-2, 0.86) * mm, v(-2.04, 0.9) * mm, v(-2.08, 0.94) * mm, v(-2.14, 0.97) * mm, v(-2.18, 1.01) * mm, v(-2.24, 1.04) * mm, v(-2.28, 1.06) * mm, v(-2.35, 1.1) * mm, v(-2.42, 1.14) * mm, v(-2.5, 1.18) * mm, v(-2.6, 1.21) * mm, v(-2.64, 1.23) * mm, v(-2.68, 1.24) * mm, v(-2.72, 1.24) * mm, v(-2.8, 1.26) * mm, v(-2.85, 1.27) * mm, v(-2.91, 1.29) * mm, v(-2.97, 1.3) * mm, v(-3.03, 1.3) * mm, v(-3.09, 1.31) * mm, v(-3.19, 1.32) * mm, v(-3.24, 1.32) * mm, v(-3.3, 1.32) * mm, v(-3.41, 1.31) * mm, v(-3.5, 1.31) * mm, v(-3.62, 1.32) * mm, v(-3.7, 1.32) * mm, v(-3.77, 1.32) * mm, v(-3.86, 1.28) * mm, v(-3.89, 1.28) * mm, v(-3.83, 1.23) * mm, v(-3.77, 1.2) * mm, v(-3.71, 1.16) * mm, v(-3.68, 1.13) * mm, v(-3.66, 1.1) * mm, v(-3.62, 1.08) * mm, v(-3.57, 1.04) * mm, v(-3.54, 1) * mm, v(-3.45, 0.93) * mm, v(-3.43, 0.9) * mm, v(-3.38, 0.82) * mm, v(-3.36, 0.77) * mm, v(-3.33, 0.71) * mm, v(-3.3, 0.66) * mm, v(-3.26, 0.57) * mm, v(-3.23, 0.5) * mm, v(-3.21, 0.43) * mm, v(-3.2, 0.32) * mm, v(-3.18, 0.27) * mm, v(-3.17, 0.22) * mm, v(-3.15, 0.15) * mm, v(-3.14, 0) * mm, v(-3.1, -0.06) * mm, v(-3.1, -0.14) * mm, v(-3.1, -0.24) * mm, v(-3.11, -0.36) * mm, v(-3.14, -0.5) * mm, v(-3.16, -0.57) * mm, v(-3.17, -0.66) * mm, v(-3.17, -0.76) * mm, v(-3.2, -0.84) * mm, v(-3.23, -0.98) * mm, v(-3.25, -1.08) * mm, v(-3.27, -1.2) * mm, v(-3.28, -1.33) * mm, v(-3.28, -1.38) * mm, v(-3.29, -1.48) * mm, v(-3.29, -1.59) * mm, v(-3.29, -1.74) * mm, v(-3.29, -1.9) * mm, v(-3.25, -2) * mm, v(-3.24, -2.1) * mm, v(-3.22, -2.17) * mm, v(-3.18, -2.27) * mm, v(-3.14, -2.43) * mm, v(-3.1, -2.48) * mm, v(-3.05, -2.58) * mm, v(-3, -2.63) * mm, v(-2.95, -2.68) * mm, v(-2.93, -2.72) * mm, v(-2.9, -2.77) * mm, v(-2.86, -2.8) * mm, v(-2.82, -2.83) * mm, v(-2.77, -2.85) * mm, v(-2.73, -2.88) * mm, v(-2.7, -2.91) * mm, v(-2.64, -2.97) * mm, v(-2.58, -3) * mm, v(-2.53, -3.02) * mm, v(-2.49, -3.03) * mm, v(-2.42, -3.08) * mm, v(-2.36, -3.12) * mm, v(-2.27, -3.15) * mm, v(-2.22, -3.17) * mm, v(-2.13, -3.21) * mm, v(-2.04, -3.23) * mm, v(-1.99, -3.24) * mm, v(-1.87, -3.28) * mm, v(-1.8, -3.28) * mm], "startDerivative": vector(-4.82, -12.37) * mm, "endDerivative": vector(13.02, 1.58) * mm});
            skFitSpline(sketch, "E127", {"points": [v(0.93, -2.74) * mm, v(0.95, -2.75) * mm], "startDerivative": vector(0.02, 0) * mm, "endDerivative": vector(0.02, 0) * mm});
            skSolve(sketch);
        }
        {
            var Q0;
            Q0 = qSketchRegion(id + "F10", true);
            extrude(context, id + "F11", {"entities" : qUnion([Q0]), "operationType" : NewBodyOperationType.ADD, "depth" : 1.27 * mm, "offsetDistance" : 25.4 * mm});
        }
    });
